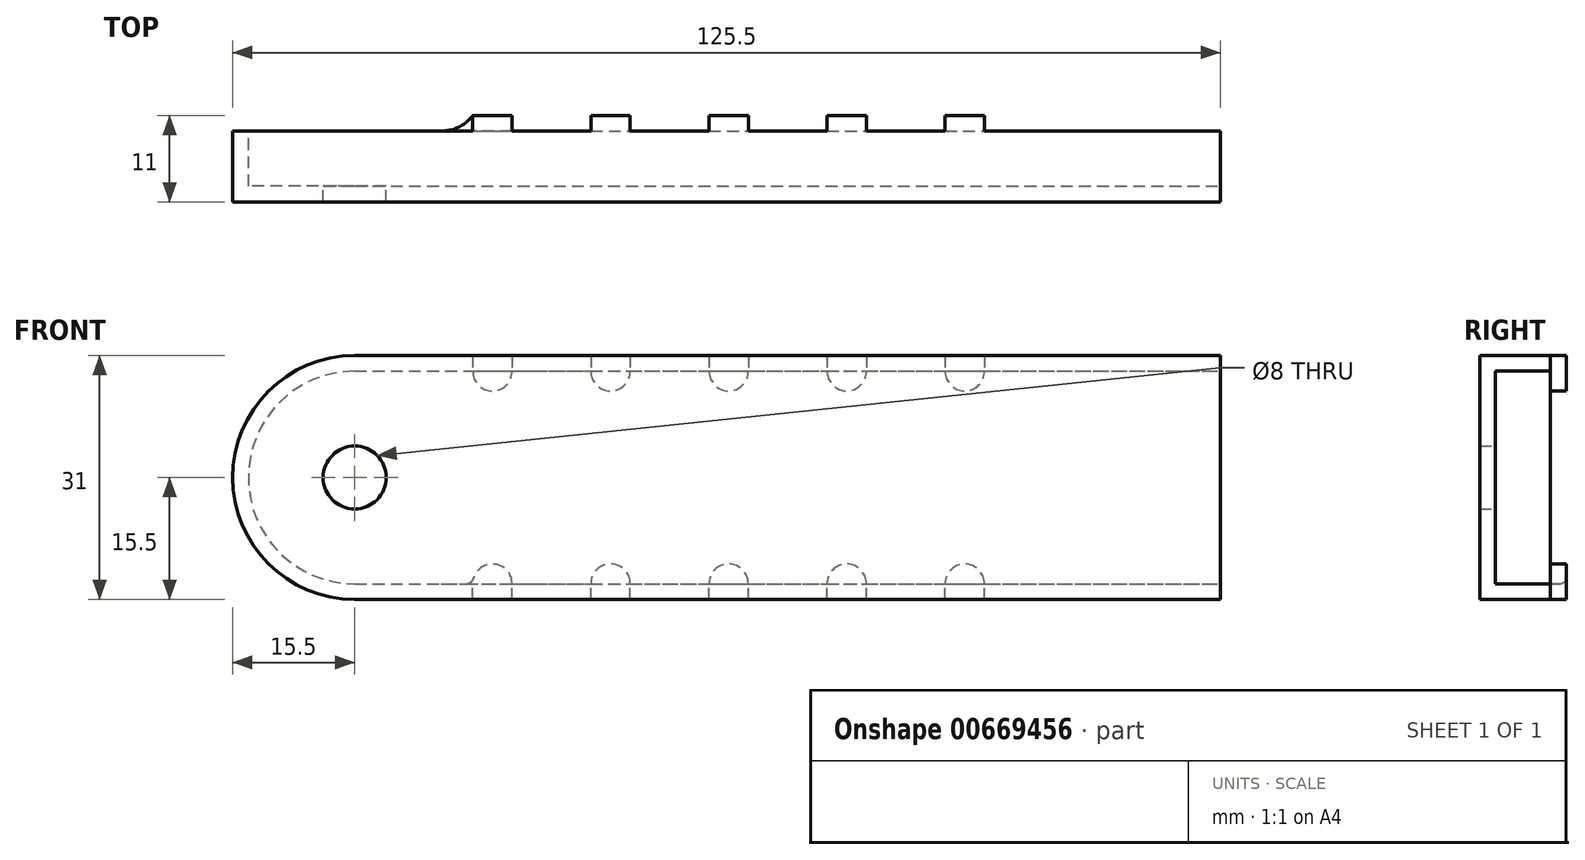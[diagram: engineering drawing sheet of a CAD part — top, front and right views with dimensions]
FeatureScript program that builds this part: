
annotation { "Feature Type Name" : "Feature", "Feature Type Description" : "" }
export const myFeature = defineFeature(function(context is Context, id is Id, definition is map)
    precondition{}
    {
        {
            var Q0;
            Q0=qCreatedBy(makeId("Front.planeOp"),FACE);
            var sketch = newSketch(context, id + "F0", { "sketchPlane" : qUnion([Q0])});
            skCircle(sketch, "E0", {"center": v(0, 0) * mm, "radius": 13.5 * mm});
            skLineSegment(sketch, "E1.bottom", {"start": v(0, 13.5) * mm, "end": v(110, 13.5) * mm});
            skLineSegment(sketch, "E1.top", {"start": v(0, -13.5) * mm, "end": v(110, -13.5) * mm});
            skLineSegment(sketch, "E1.left", {"start": v(0, 13.5) * mm, "end": v(0, -13.5) * mm});
            skLineSegment(sketch, "E1.right", {"start": v(110, 13.5) * mm, "end": v(110, -13.5) * mm});
            skSolve(sketch);
        }
        {
            var Q0;
            Q0 = qSketchRegion(id + "F0", true);
            extrude(context, id + "F1", {"entities" : qUnion([Q0]), "depth" : 7 * mm, "offsetDistance" : 25 * mm});
        }
        {
            var Q0;
            Q0=makeQuery(id+"F1.opExtrude","CAP_FACE",FACE,{"disambiguationData":[OSD([sQuery(id+"F0.wireOp",EDGE,"E0"),sQuery(id+"F0.wireOp",EDGE,"E1.bottom"),sQuery(id+"F0.wireOp",EDGE,"E1.top"),sQuery(id+"F0.wireOp",EDGE,"E1.right")])],"isStart":true});
            var Q1;
            Q1=makeQuery(id+"F1.opExtrude","SWEPT_FACE",FACE,{"disambiguationData":[OSD([sQuery(id+"F0.wireOp",EDGE,"E1.right")])]});
            shell(context, id + "F2", {"entities" : qUnion([Q0, Q1]), "thickness" : 2 * mm, "oppositeDirection" : true});
        }
        {
            var Q0;
            Q0=sQuery(id+"F0.wireOp",VERTEX,"E0.center");
            var Q1;
            Q1=makeQuery(id+"F1.opExtrude","SWEPT_BODY",BODY,{"disambiguationData":[OSD([sQuery(id+"F0.wireOp",EDGE,"E0"),sQuery(id+"F0.wireOp",EDGE,"E1.bottom"),sQuery(id+"F0.wireOp",EDGE,"E1.top"),sQuery(id+"F0.wireOp",EDGE,"E1.right")])]});
            hole(context, id + "F3", {"style" : HoleStyle.SIMPLE, "endStyle" : HoleEndStyle.THROUGH, "oppositeDirection" : true, "holeDiameter" : 8 * mm, "majorDiameter" : 5 * mm, "isTappedThrough" : true, "tappedDepth" : 12.7 * mm, "tapClearance" : 3, "startFromSketch" : true, "locations" : qUnion([Q0]), "scope" : qUnion([Q1])});
        }
        {
            var Q0;
            Q0=makeQuery(id+"F1.opExtrude","CAP_FACE",FACE,{"disambiguationData":[OSD([sQuery(id+"F0.wireOp",EDGE,"E0"),sQuery(id+"F0.wireOp",EDGE,"E1.bottom"),sQuery(id+"F0.wireOp",EDGE,"E1.top"),sQuery(id+"F0.wireOp",EDGE,"E1.right")])],"isStart":true});
            var sketch = newSketch(context, id + "F4", { "sketchPlane" : qUnion([Q0])});
            skLineSegment(sketch, "E2.bottom", {"start": v(-15, -15.5) * mm, "end": v(-20, -15.5) * mm});
            skLineSegment(sketch, "E2.top", {"start": v(-15, -13.5) * mm, "end": v(-20, -13.5) * mm});
            skLineSegment(sketch, "E2.left", {"start": v(-15, -15.5) * mm, "end": v(-15, -13.5) * mm});
            skLineSegment(sketch, "E2.right", {"start": v(-20, -15.5) * mm, "end": v(-20, -13.5) * mm});
            skArc(sketch, "E3", {"start": v(-15, -13.5) * mm, "mid": v(-17.5, -11) * mm, "end": v(-20, -13.5) * mm});
            skLineSegment(sketch, "E4.1.0.0", {"start": v(-30, -15.5) * mm, "end": v(-35, -15.5) * mm});
            skLineSegment(sketch, "E4.1.0.1", {"start": v(-30, -13.5) * mm, "end": v(-35, -13.5) * mm});
            skLineSegment(sketch, "E4.1.0.2", {"start": v(-30, -15.5) * mm, "end": v(-30, -13.5) * mm});
            skLineSegment(sketch, "E4.1.0.3", {"start": v(-35, -15.5) * mm, "end": v(-35, -13.5) * mm});
            skArc(sketch, "E4.1.0.4", {"start": v(-30, -13.5) * mm, "mid": v(-32.5, -11) * mm, "end": v(-35, -13.5) * mm});
            skLineSegment(sketch, "E4.2.0.0", {"start": v(-45, -15.5) * mm, "end": v(-50, -15.5) * mm});
            skLineSegment(sketch, "E4.2.0.1", {"start": v(-45, -13.5) * mm, "end": v(-50, -13.5) * mm});
            skLineSegment(sketch, "E4.2.0.2", {"start": v(-45, -15.5) * mm, "end": v(-45, -13.5) * mm});
            skLineSegment(sketch, "E4.2.0.3", {"start": v(-50, -15.5) * mm, "end": v(-50, -13.5) * mm});
            skArc(sketch, "E4.2.0.4", {"start": v(-45, -13.5) * mm, "mid": v(-47.5, -11) * mm, "end": v(-50, -13.5) * mm});
            skLineSegment(sketch, "E4.3.0.0", {"start": v(-60, -15.5) * mm, "end": v(-65, -15.5) * mm});
            skLineSegment(sketch, "E4.3.0.1", {"start": v(-60, -13.5) * mm, "end": v(-65, -13.5) * mm});
            skLineSegment(sketch, "E4.3.0.2", {"start": v(-60, -15.5) * mm, "end": v(-60, -13.5) * mm});
            skLineSegment(sketch, "E4.3.0.3", {"start": v(-65, -15.5) * mm, "end": v(-65, -13.5) * mm});
            skArc(sketch, "E4.3.0.4", {"start": v(-60, -13.5) * mm, "mid": v(-62.5, -11) * mm, "end": v(-65, -13.5) * mm});
            skLineSegment(sketch, "E4.4.0.0", {"start": v(-75, -15.5) * mm, "end": v(-80, -15.5) * mm});
            skLineSegment(sketch, "E4.4.0.1", {"start": v(-75, -13.5) * mm, "end": v(-80, -13.5) * mm});
            skLineSegment(sketch, "E4.4.0.2", {"start": v(-75, -15.5) * mm, "end": v(-75, -13.5) * mm});
            skLineSegment(sketch, "E4.4.0.3", {"start": v(-80, -15.5) * mm, "end": v(-80, -13.5) * mm});
            skArc(sketch, "E4.4.0.4", {"start": v(-75, -13.5) * mm, "mid": v(-77.5, -11) * mm, "end": v(-80, -13.5) * mm});
            skLineSegment(sketch, "E4.direction1", {"start": v(-20, -15.5) * mm, "end": v(-35, -15.5) * mm, "construction": true});
            skLineSegment(sketch, "E5.bottom", {"start": v(-15, 15.5) * mm, "end": v(-20, 15.5) * mm});
            skLineSegment(sketch, "E5.top", {"start": v(-15, 13.5) * mm, "end": v(-20, 13.5) * mm});
            skLineSegment(sketch, "E5.left", {"start": v(-15, 15.5) * mm, "end": v(-15, 13.5) * mm});
            skLineSegment(sketch, "E5.right", {"start": v(-20, 15.5) * mm, "end": v(-20, 13.5) * mm});
            skArc(sketch, "E6", {"start": v(-20, 13.5) * mm, "mid": v(-17.5, 11) * mm, "end": v(-15, 13.5) * mm});
            skLineSegment(sketch, "E7.1.0.0", {"start": v(-30, 13.5) * mm, "end": v(-35, 13.5) * mm});
            skLineSegment(sketch, "E7.1.0.1", {"start": v(-30, 15.5) * mm, "end": v(-35, 15.5) * mm});
            skArc(sketch, "E7.1.0.2", {"start": v(-35, 13.5) * mm, "mid": v(-32.5, 11) * mm, "end": v(-30, 13.5) * mm});
            skLineSegment(sketch, "E7.1.0.3", {"start": v(-35, 15.5) * mm, "end": v(-35, 13.5) * mm});
            skLineSegment(sketch, "E7.1.0.4", {"start": v(-30, 15.5) * mm, "end": v(-30, 13.5) * mm});
            skLineSegment(sketch, "E7.2.0.0", {"start": v(-45, 13.5) * mm, "end": v(-50, 13.5) * mm});
            skLineSegment(sketch, "E7.2.0.1", {"start": v(-45, 15.5) * mm, "end": v(-50, 15.5) * mm});
            skArc(sketch, "E7.2.0.2", {"start": v(-50, 13.5) * mm, "mid": v(-47.5, 11) * mm, "end": v(-45, 13.5) * mm});
            skLineSegment(sketch, "E7.2.0.3", {"start": v(-50, 15.5) * mm, "end": v(-50, 13.5) * mm});
            skLineSegment(sketch, "E7.2.0.4", {"start": v(-45, 15.5) * mm, "end": v(-45, 13.5) * mm});
            skLineSegment(sketch, "E7.3.0.0", {"start": v(-60, 13.5) * mm, "end": v(-65, 13.5) * mm});
            skLineSegment(sketch, "E7.3.0.1", {"start": v(-60, 15.5) * mm, "end": v(-65, 15.5) * mm});
            skArc(sketch, "E7.3.0.2", {"start": v(-65, 13.5) * mm, "mid": v(-62.5, 11) * mm, "end": v(-60, 13.5) * mm});
            skLineSegment(sketch, "E7.3.0.3", {"start": v(-65, 15.5) * mm, "end": v(-65, 13.5) * mm});
            skLineSegment(sketch, "E7.3.0.4", {"start": v(-60, 15.5) * mm, "end": v(-60, 13.5) * mm});
            skLineSegment(sketch, "E7.4.0.0", {"start": v(-75, 13.5) * mm, "end": v(-80, 13.5) * mm});
            skLineSegment(sketch, "E7.4.0.1", {"start": v(-75, 15.5) * mm, "end": v(-80, 15.5) * mm});
            skArc(sketch, "E7.4.0.2", {"start": v(-80, 13.5) * mm, "mid": v(-77.5, 11) * mm, "end": v(-75, 13.5) * mm});
            skLineSegment(sketch, "E7.4.0.3", {"start": v(-80, 15.5) * mm, "end": v(-80, 13.5) * mm});
            skLineSegment(sketch, "E7.4.0.4", {"start": v(-75, 15.5) * mm, "end": v(-75, 13.5) * mm});
            skLineSegment(sketch, "E7.direction1", {"start": v(-20, 13.5) * mm, "end": v(-35, 13.5) * mm, "construction": true});
            skSolve(sketch);
        }
        {
            var Q0;
            Q0 = qSketchRegion(id + "F4", true);
            extrude(context, id + "F5", {"entities" : qUnion([Q0]), "operationType" : NewBodyOperationType.ADD, "depth" : 2 * mm, "offsetDistance" : 25 * mm});
        }
        {
            var Q0;
            {var subQ0=sQuery(id+"F4.wireOp",EDGE,"WJNgTTKY-IQkI-YbYd-H46O-tygjUo5JVjjR.right");Q0=makeQuery(id+"F5.boolean.opBoolean","SPLIT",EDGE,{"disambiguationData":[topologyDisambiguationEdgeConnected([makeQuery(id+"F1.opExtrude","CAP_FACE",FACE,{"disambiguationData":[OSD([sQuery(id+"F0.wireOp",EDGE,"E0"),sQuery(id+"F0.wireOp",EDGE,"E1.bottom"),sQuery(id+"F0.wireOp",EDGE,"E1.top"),sQuery(id+"F0.wireOp",EDGE,"E1.right")])],"isStart":true})])],"derivedFrom":makeQuery(id+"F5.opExtrude","CAP_EDGE",EDGE,{"disambiguationData":[OSD([subQ0])],"isStart":true})});}
            var Q1;
            {var subQ0=sQuery(id+"F4.wireOp",EDGE,"XvaurJLT-M8K7-hR2b-WGb5-wn7II6dvVY4X.right");Q1=makeQuery(id+"F5.boolean.opBoolean","SPLIT",EDGE,{"disambiguationData":[topologyDisambiguationEdgeConnected([makeQuery(id+"F1.opExtrude","CAP_FACE",FACE,{"disambiguationData":[OSD([sQuery(id+"F0.wireOp",EDGE,"E0"),sQuery(id+"F0.wireOp",EDGE,"E1.bottom"),sQuery(id+"F0.wireOp",EDGE,"E1.top"),sQuery(id+"F0.wireOp",EDGE,"E1.right")])],"isStart":true})])],"derivedFrom":makeQuery(id+"F5.opExtrude","CAP_EDGE",EDGE,{"disambiguationData":[OSD([subQ0])],"isStart":true})});}
            var Q2;
            {var subQ0=sQuery(id+"F4.wireOp",EDGE,"E2.right");Q2=makeQuery(id+"F5.boolean.opBoolean","SPLIT",EDGE,{"disambiguationData":[topologyDisambiguationEdgeConnected([makeQuery(id+"F1.opExtrude","CAP_FACE",FACE,{"disambiguationData":[OSD([sQuery(id+"F0.wireOp",EDGE,"E0"),sQuery(id+"F0.wireOp",EDGE,"E1.bottom"),sQuery(id+"F0.wireOp",EDGE,"E1.top"),sQuery(id+"F0.wireOp",EDGE,"E1.right")])],"isStart":true})])],"derivedFrom":makeQuery(id+"F5.opExtrude","CAP_EDGE",EDGE,{"disambiguationData":[OSD([subQ0])],"isStart":true})});}
            var Q3;
            {var subQ0=sQuery(id+"F4.wireOp",EDGE,"uWLqeNH7-OiFK-N74I-lnwu-8SltvSWOjEbD.right");Q3=makeQuery(id+"F5.boolean.opBoolean","SPLIT",EDGE,{"disambiguationData":[topologyDisambiguationEdgeConnected([makeQuery(id+"F1.opExtrude","CAP_FACE",FACE,{"disambiguationData":[OSD([sQuery(id+"F0.wireOp",EDGE,"E0"),sQuery(id+"F0.wireOp",EDGE,"E1.bottom"),sQuery(id+"F0.wireOp",EDGE,"E1.top"),sQuery(id+"F0.wireOp",EDGE,"E1.right")])],"isStart":true})])],"derivedFrom":makeQuery(id+"F5.opExtrude","CAP_EDGE",EDGE,{"disambiguationData":[OSD([subQ0])],"isStart":true})});}
            var Q4;
            {var subQ0=sQuery(id+"F4.wireOp",EDGE,"61PmLzjh-etuL-wPcE-S0LD-THnsS4RU3OpW.right");Q4=makeQuery(id+"F5.boolean.opBoolean","SPLIT",EDGE,{"disambiguationData":[topologyDisambiguationEdgeConnected([makeQuery(id+"F1.opExtrude","CAP_FACE",FACE,{"disambiguationData":[OSD([sQuery(id+"F0.wireOp",EDGE,"E0"),sQuery(id+"F0.wireOp",EDGE,"E1.bottom"),sQuery(id+"F0.wireOp",EDGE,"E1.top"),sQuery(id+"F0.wireOp",EDGE,"E1.right")])],"isStart":true})])],"derivedFrom":makeQuery(id+"F5.opExtrude","CAP_EDGE",EDGE,{"disambiguationData":[OSD([subQ0])],"isStart":true})});}
            var Q5;
            {var subQ0=sQuery(id+"F4.wireOp",EDGE,"oo0OOwAg-2Pof-U5TH-na0j-kpJhm6oW7tAE.right");Q5=makeQuery(id+"F5.boolean.opBoolean","SPLIT",EDGE,{"disambiguationData":[topologyDisambiguationEdgeConnected([makeQuery(id+"F1.opExtrude","CAP_FACE",FACE,{"disambiguationData":[OSD([sQuery(id+"F0.wireOp",EDGE,"E0"),sQuery(id+"F0.wireOp",EDGE,"E1.bottom"),sQuery(id+"F0.wireOp",EDGE,"E1.top"),sQuery(id+"F0.wireOp",EDGE,"E1.right")])],"isStart":true})])],"derivedFrom":makeQuery(id+"F5.opExtrude","CAP_EDGE",EDGE,{"disambiguationData":[OSD([subQ0])],"isStart":true})});}
            var Q6;
            {var subQ0=sQuery(id+"F4.wireOp",EDGE,"61PmLzjh-etuL-wPcE-S0LD-THnsS4RU3OpW.left");Q6=makeQuery(id+"F5.boolean.opBoolean","SPLIT",EDGE,{"disambiguationData":[topologyDisambiguationEdgeConnected([makeQuery(id+"F1.opExtrude","CAP_FACE",FACE,{"disambiguationData":[OSD([sQuery(id+"F0.wireOp",EDGE,"E0"),sQuery(id+"F0.wireOp",EDGE,"E1.bottom"),sQuery(id+"F0.wireOp",EDGE,"E1.top"),sQuery(id+"F0.wireOp",EDGE,"E1.right")])],"isStart":true})])],"derivedFrom":makeQuery(id+"F5.opExtrude","CAP_EDGE",EDGE,{"disambiguationData":[OSD([subQ0])],"isStart":true})});}
            var Q7;
            {var subQ0=sQuery(id+"F4.wireOp",EDGE,"E2.left");Q7=makeQuery(id+"F5.boolean.opBoolean","SPLIT",EDGE,{"disambiguationData":[topologyDisambiguationEdgeConnected([makeQuery(id+"F1.opExtrude","CAP_FACE",FACE,{"disambiguationData":[OSD([sQuery(id+"F0.wireOp",EDGE,"E0"),sQuery(id+"F0.wireOp",EDGE,"E1.bottom"),sQuery(id+"F0.wireOp",EDGE,"E1.top"),sQuery(id+"F0.wireOp",EDGE,"E1.right")])],"isStart":true})])],"derivedFrom":makeQuery(id+"F5.opExtrude","CAP_EDGE",EDGE,{"disambiguationData":[OSD([subQ0])],"isStart":true})});}
            var Q8;
            {var subQ0=sQuery(id+"F4.wireOp",EDGE,"uWLqeNH7-OiFK-N74I-lnwu-8SltvSWOjEbD.left");Q8=makeQuery(id+"F5.boolean.opBoolean","SPLIT",EDGE,{"disambiguationData":[topologyDisambiguationEdgeConnected([makeQuery(id+"F1.opExtrude","CAP_FACE",FACE,{"disambiguationData":[OSD([sQuery(id+"F0.wireOp",EDGE,"E0"),sQuery(id+"F0.wireOp",EDGE,"E1.bottom"),sQuery(id+"F0.wireOp",EDGE,"E1.top"),sQuery(id+"F0.wireOp",EDGE,"E1.right")])],"isStart":true})])],"derivedFrom":makeQuery(id+"F5.opExtrude","CAP_EDGE",EDGE,{"disambiguationData":[OSD([subQ0])],"isStart":true})});}
            var Q9;
            {var subQ0=sQuery(id+"F4.wireOp",EDGE,"XvaurJLT-M8K7-hR2b-WGb5-wn7II6dvVY4X.left");Q9=makeQuery(id+"F5.boolean.opBoolean","SPLIT",EDGE,{"disambiguationData":[topologyDisambiguationEdgeConnected([makeQuery(id+"F1.opExtrude","CAP_FACE",FACE,{"disambiguationData":[OSD([sQuery(id+"F0.wireOp",EDGE,"E0"),sQuery(id+"F0.wireOp",EDGE,"E1.bottom"),sQuery(id+"F0.wireOp",EDGE,"E1.top"),sQuery(id+"F0.wireOp",EDGE,"E1.right")])],"isStart":true})])],"derivedFrom":makeQuery(id+"F5.opExtrude","CAP_EDGE",EDGE,{"disambiguationData":[OSD([subQ0])],"isStart":true})});}
            var Q10;
            {var subQ0=sQuery(id+"F4.wireOp",EDGE,"WJNgTTKY-IQkI-YbYd-H46O-tygjUo5JVjjR.left");Q10=makeQuery(id+"F5.boolean.opBoolean","SPLIT",EDGE,{"disambiguationData":[topologyDisambiguationEdgeConnected([makeQuery(id+"F1.opExtrude","CAP_FACE",FACE,{"disambiguationData":[OSD([sQuery(id+"F0.wireOp",EDGE,"E0"),sQuery(id+"F0.wireOp",EDGE,"E1.bottom"),sQuery(id+"F0.wireOp",EDGE,"E1.top"),sQuery(id+"F0.wireOp",EDGE,"E1.right")])],"isStart":true})])],"derivedFrom":makeQuery(id+"F5.opExtrude","CAP_EDGE",EDGE,{"disambiguationData":[OSD([subQ0])],"isStart":true})});}
            var Q11;
            {var subQ0=sQuery(id+"F4.wireOp",EDGE,"oo0OOwAg-2Pof-U5TH-na0j-kpJhm6oW7tAE.left");Q11=makeQuery(id+"F5.boolean.opBoolean","SPLIT",EDGE,{"disambiguationData":[topologyDisambiguationEdgeConnected([makeQuery(id+"F1.opExtrude","CAP_FACE",FACE,{"disambiguationData":[OSD([sQuery(id+"F0.wireOp",EDGE,"E0"),sQuery(id+"F0.wireOp",EDGE,"E1.bottom"),sQuery(id+"F0.wireOp",EDGE,"E1.top"),sQuery(id+"F0.wireOp",EDGE,"E1.right")])],"isStart":true})])],"derivedFrom":makeQuery(id+"F5.opExtrude","CAP_EDGE",EDGE,{"disambiguationData":[OSD([subQ0])],"isStart":true})});}
            fillet(context, id + "F6", {"entities" : qUnion([Q0, Q1, Q2, Q3, Q4, Q5, Q6, Q7, Q8, Q9, Q10, Q11]), "radius" : 5 * mm, "tangentPropagation" : true, "allowEdgeOverflow" : false});
        }
        {
            var Q0;
            Q0=makeQuery(id+"F5.opExtrude","SWEPT_EDGE",EDGE,{"disambiguationData":[OSD([sQuery(id+"F4.wireOp",EDGE,"oo0OOwAg-2Pof-U5TH-na0j-kpJhm6oW7tAE.top"),sQuery(id+"F4.wireOp",EDGE,"oo0OOwAg-2Pof-U5TH-na0j-kpJhm6oW7tAE.right")])]});
            var Q1;
            Q1=makeQuery(id+"F5.opExtrude","SWEPT_EDGE",EDGE,{"disambiguationData":[OSD([sQuery(id+"F4.wireOp",EDGE,"oo0OOwAg-2Pof-U5TH-na0j-kpJhm6oW7tAE.top"),sQuery(id+"F4.wireOp",EDGE,"oo0OOwAg-2Pof-U5TH-na0j-kpJhm6oW7tAE.left")])]});
            var Q2;
            Q2=makeQuery(id+"F5.opExtrude","SWEPT_EDGE",EDGE,{"disambiguationData":[OSD([sQuery(id+"F4.wireOp",EDGE,"uWLqeNH7-OiFK-N74I-lnwu-8SltvSWOjEbD.top"),sQuery(id+"F4.wireOp",EDGE,"uWLqeNH7-OiFK-N74I-lnwu-8SltvSWOjEbD.right")])]});
            var Q3;
            Q3=makeQuery(id+"F5.opExtrude","SWEPT_EDGE",EDGE,{"disambiguationData":[OSD([sQuery(id+"F4.wireOp",EDGE,"uWLqeNH7-OiFK-N74I-lnwu-8SltvSWOjEbD.top"),sQuery(id+"F4.wireOp",EDGE,"uWLqeNH7-OiFK-N74I-lnwu-8SltvSWOjEbD.left")])]});
            var Q4;
            Q4=makeQuery(id+"F5.opExtrude","SWEPT_EDGE",EDGE,{"disambiguationData":[OSD([sQuery(id+"F4.wireOp",EDGE,"E2.top"),sQuery(id+"F4.wireOp",EDGE,"E2.right")])]});
            var Q5;
            Q5=makeQuery(id+"F5.opExtrude","SWEPT_EDGE",EDGE,{"disambiguationData":[OSD([sQuery(id+"F4.wireOp",EDGE,"E2.top"),sQuery(id+"F4.wireOp",EDGE,"E2.left")])]});
            var Q6;
            Q6=makeQuery(id+"F5.opExtrude","SWEPT_EDGE",EDGE,{"disambiguationData":[OSD([sQuery(id+"F4.wireOp",EDGE,"WJNgTTKY-IQkI-YbYd-H46O-tygjUo5JVjjR.top"),sQuery(id+"F4.wireOp",EDGE,"WJNgTTKY-IQkI-YbYd-H46O-tygjUo5JVjjR.right")])]});
            var Q7;
            Q7=makeQuery(id+"F5.opExtrude","SWEPT_EDGE",EDGE,{"disambiguationData":[OSD([sQuery(id+"F4.wireOp",EDGE,"WJNgTTKY-IQkI-YbYd-H46O-tygjUo5JVjjR.top"),sQuery(id+"F4.wireOp",EDGE,"WJNgTTKY-IQkI-YbYd-H46O-tygjUo5JVjjR.left")])]});
            var Q8;
            Q8=makeQuery(id+"F5.opExtrude","SWEPT_EDGE",EDGE,{"disambiguationData":[OSD([sQuery(id+"F4.wireOp",EDGE,"XvaurJLT-M8K7-hR2b-WGb5-wn7II6dvVY4X.top"),sQuery(id+"F4.wireOp",EDGE,"XvaurJLT-M8K7-hR2b-WGb5-wn7II6dvVY4X.right")])]});
            var Q9;
            Q9=makeQuery(id+"F5.opExtrude","SWEPT_EDGE",EDGE,{"disambiguationData":[OSD([sQuery(id+"F4.wireOp",EDGE,"XvaurJLT-M8K7-hR2b-WGb5-wn7II6dvVY4X.top"),sQuery(id+"F4.wireOp",EDGE,"XvaurJLT-M8K7-hR2b-WGb5-wn7II6dvVY4X.left")])]});
            var Q10;
            Q10=makeQuery(id+"F5.opExtrude","SWEPT_EDGE",EDGE,{"disambiguationData":[OSD([sQuery(id+"F4.wireOp",EDGE,"61PmLzjh-etuL-wPcE-S0LD-THnsS4RU3OpW.top"),sQuery(id+"F4.wireOp",EDGE,"61PmLzjh-etuL-wPcE-S0LD-THnsS4RU3OpW.right")])]});
            var Q11;
            Q11=makeQuery(id+"F5.opExtrude","SWEPT_EDGE",EDGE,{"disambiguationData":[OSD([sQuery(id+"F4.wireOp",EDGE,"61PmLzjh-etuL-wPcE-S0LD-THnsS4RU3OpW.top"),sQuery(id+"F4.wireOp",EDGE,"61PmLzjh-etuL-wPcE-S0LD-THnsS4RU3OpW.left")])]});
            fillet(context, id + "F7", {"entities" : qUnion([Q0, Q1, Q2, Q3, Q4, Q5, Q6, Q7, Q8, Q9, Q10, Q11]), "radius" : 1 * mm, "tangentPropagation" : true, "allowEdgeOverflow" : false});
        }
    });
